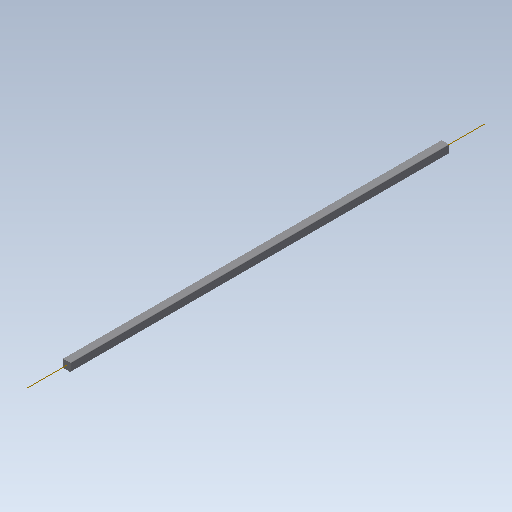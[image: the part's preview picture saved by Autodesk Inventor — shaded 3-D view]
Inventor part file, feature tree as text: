
AUTODESK INVENTOR PART (.ipt)
format: ipt  version: 2020 (Build 240168000, 168)  size: 164,864 bytes
history: native  units: in
note: dims shown in document units (in); Inventor stores cm internally (conversion verified against a paired STEP export)
features: other x5, extrude x1, imported_body x1, sketch x1
ambient origin geometry x8: Origin, YZ Plane, XZ Plane, XY Plane, X Axis, Y Axis, Z Axis, Center Point
bodies: Body1 (feature_tree)
feature tree (8):
  parser-record x1  (decoder bookkeeping rows leaked as tree rows — omitted from the tree; the rows remain in map.json)
  other  "Shaft"
  extrude  "length cut"  Depth=6.0in
  other  "front plane"
  imported_body  "Base1"
  sketch  "Sketch1"  dims[d1=0.0in d2=6.0in d3=0.0in d4=0.0in d5=0.0in]
  other  "main axis"
  other  "back plane"
